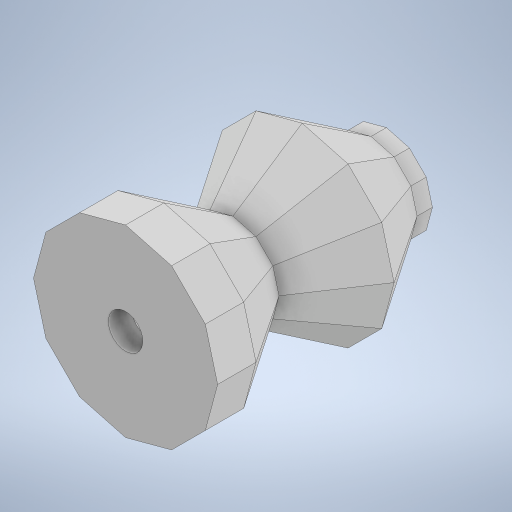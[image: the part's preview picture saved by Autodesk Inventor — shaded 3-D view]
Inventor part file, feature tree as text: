
AUTODESK INVENTOR PART (.ipt)
format: ipt  version: 2023 (Build 270158000, 158)  size: 353,792 bytes
history: native  units: in
note: dims shown in document units (in); Inventor stores cm internally (conversion verified against a paired STEP export)
features: sketch x6, extrude x4, projected_geometry x3, other x2, mirror x2, loft x1, shell x1
ambient origin geometry x8: Origin, YZ Plane, XZ Plane, XY Plane, X Axis, Y Axis, Z Axis, Center Point
bodies: Body1 (feature_tree)
feature tree (19):
  other  "솔리드1"
  sketch  "스케치1"
  other  "작업 평면1"
  loft  "로프트1"
  mirror  "미러1"
  mirror  "미러2"
  extrude  "돌출1"  Depth=0.3543in
  shell  "쉘1"  Thickness=0.4724in
  extrude  "돌출2"  TaperAngle=0.0deg  [1 undecoded]
  extrude  "돌출3"  TaperAngle=0.0deg  [1 undecoded]
  extrude  "돌출4"  Depth=0.0984in TaperAngle=0.0deg
  sketch  "스케치2"
  sketch  "스케치3"
  projected_geometry  "투영된 루프1"
  sketch  "스케치4"
  projected_geometry  "투영된 루프2"
  sketch  "스케치5"
  sketch  "스케치6"
  projected_geometry  "투영된 루프3"
note: 2 required parameter values undecoded (feature->parameter linkage not recoverable at this tier; creation-order binding heuristic only, values carry confidence <= 0.55)
